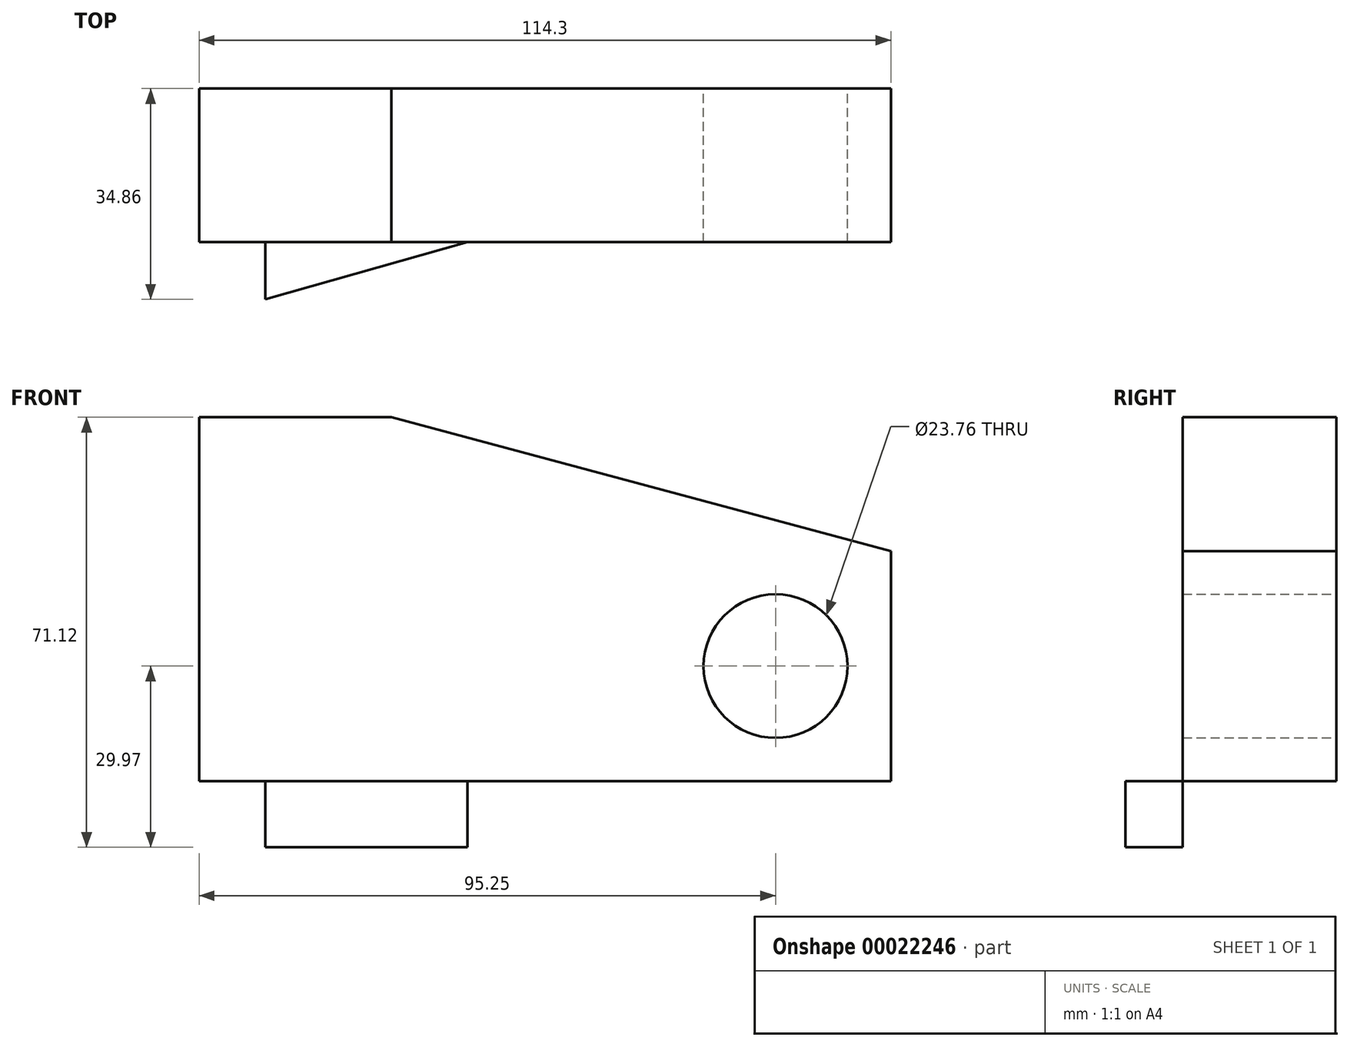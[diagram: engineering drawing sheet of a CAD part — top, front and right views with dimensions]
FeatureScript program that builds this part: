
annotation { "Feature Type Name" : "Feature", "Feature Type Description" : "" }
export const myFeature = defineFeature(function(context is Context, id is Id, definition is map)
    precondition{}
    {
        {
            var Q0;
            Q0=qCreatedBy(makeId("Front.planeOp"),FACE);
            var sketch = newSketch(context, id + "F0", { "sketchPlane" : qUnion([Q0])});
            skLineSegment(sketch, "E0.bottom", {"start": v(0, 0) * mm, "end": v(-114.3, 0) * mm});
            skLineSegment(sketch, "E0.top", {"start": v(-82.55, 60.2) * mm, "end": v(-114.3, 60.2) * mm});
            skLineSegment(sketch, "E0.left", {"start": v(0, 0) * mm, "end": v(0, 60.2) * mm});
            skLineSegment(sketch, "E0.right", {"start": v(-114.3, 0) * mm, "end": v(-114.3, 60.2) * mm});
            skLineSegment(sketch, "E1", {"start": v(-82.55, 60.2) * mm, "end": v(0, 38.08) * mm});
            skCircle(sketch, "E2", {"center": v(-19.05, 19.05) * mm, "radius": 11.88 * mm});
            skLineSegment(sketch, "E3", {"start": v(-103.38, 0) * mm, "end": v(-103.38, 12.35) * mm});
            skLineSegment(sketch, "E4", {"start": v(-103.38, 12.35) * mm, "end": v(-69.73, 12.35) * mm});
            skLineSegment(sketch, "E5", {"start": v(-69.73, 12.35) * mm, "end": v(-69.73, 0) * mm});
            skSolve(sketch);
        }
        {
            var Q0;
            {var subQ1=sQuery(id+"F0.wireOp",EDGE,"679ed507-37e2-4c1f-b376-8a945d00b68c");Q0=makeQuery(id+"F0.imprint","IMPRINT",FACE,{"disambiguationData":[TD([[makeQuery(id+"F0.imprint","IMPRINT",EDGE,{"derivedFrom":subQ1}),-1.0]])]});}
            var Q1;
            {var subQ3=sQuery(id+"F0.wireOp",EDGE,"E0.bottom");Q1=makeQuery(id+"F0.imprint","IMPRINT",FACE,{"disambiguationData":[TD([[makeQuery(id+"F0.imprint","IMPRINT",EDGE,{"derivedFrom":subQ3}),-1.0]])]});}
            extrude(context, id + "F1", {"entities" : qUnion([Q0, Q1]), "depth" : 10.92 * mm});
        }
        {
            var Q0;
            Q0 = qSketchRegion(id + "F0", true);
            extrude(context, id + "F2", {"entities" : qUnion([Q0]), "operationType" : NewBodyOperationType.ADD, "depth" : 25.4 * mm});
        }
        {
            var Q0;
            Q0 = qSketchRegion(id + "F0", true);
            extrude(context, id + "F3", {"entities" : qUnion([Q0]), "operationType" : NewBodyOperationType.ADD, "depth" : 25.4 * mm});
        }
        {
            var Q0;
            Q0=makeQuery(id+"F1.opExtrude","CAP_FACE",FACE,{"disambiguationData":[OSD([sQuery(id+"F0.wireOp",EDGE,"E0.bottom"),sQuery(id+"F0.wireOp",EDGE,"E0.top"),sQuery(id+"F0.wireOp",EDGE,"E0.left"),sQuery(id+"F0.wireOp",EDGE,"E0.right"),sQuery(id+"F0.wireOp",EDGE,"E1"),sQuery(id+"F0.wireOp",EDGE,"E2")])],"isStart":false});
            var Q1;
            Q1 = qSketchRegion(id + "F0", true);
            extrude(context, id + "F4", {"entities" : qUnion([Q0, Q1]), "operationType" : NewBodyOperationType.ADD, "depth" : 25.4 * mm});
        }
        {
            var Q0;
            {var subQ0=sQuery(id+"F0.wireOp",EDGE,"E0.bottom");Q0=makeQuery(id+"F2.boolean.opBoolean","MERGE",FACE,{"derivedFrom":[makeQuery(id+"F1.opExtrude","SWEPT_FACE",FACE,{"disambiguationData":[OSD([subQ0])]}),makeQuery(id+"F2.opExtrude","SWEPT_FACE",FACE,{"disambiguationData":[OSD([subQ0])]})]});}
            var sketch = newSketch(context, id + "F5", { "sketchPlane" : qUnion([Q0])});
            skLineSegment(sketch, "E6.bottom", {"start": v(-103.38, 25.4) * mm, "end": v(-69.92, 25.4) * mm});
            skLineSegment(sketch, "E6.left", {"start": v(-103.38, 25.4) * mm, "end": v(-103.38, 34.86) * mm});
            skLineSegment(sketch, "E7", {"start": v(-103.38, 34.86) * mm, "end": v(-69.92, 25.4) * mm});
            skSolve(sketch);
        }
        {
            var Q0;
            Q0 = qSketchRegion(id + "F5", true);
            extrude(context, id + "F6", {"entities" : qUnion([Q0]), "depth" : 10.92 * mm});
        }
        {
            var Q0;
            {var subQ1=sQuery(id+"F0.wireOp",EDGE,"E3");Q0=makeQuery(id+"F0.imprint","IMPRINT",FACE,{"disambiguationData":[TD([[makeQuery(id+"F0.imprint","IMPRINT",EDGE,{"derivedFrom":subQ1}),-1.0]])]});}
            extrude(context, id + "F7", {"entities" : qUnion([Q0]), "operationType" : NewBodyOperationType.ADD, "depth" : 25.4 * mm});
        }
    });
